# Revit family: Lavabo için Geberit sifon, yatay çıkış_PRO_145876
name_source: partatom
category: Pipe Fittings
revit_build: Autodesk Revit 2018 (Build: 20190510_1515(x64)
units: mm (PartAtom-declared; Revit-internal decimal feet)

## family parameters
Always vertical = Yes
Cut with Voids When Loaded = No
OmniClass Number = 23.60.30.11.14
OmniClass Title = Pipework Fittings
Part Type = Multi Port
Round Connector Dimension = Use Diameter
Shared = No
Work Plane-Based = No

## types (2) — shared parameters
Application purposes = Lavabolar için
Application range = Waste fittings
BIM Content Version = GEB MG 1.2
BIM Content revision date = 2020.04.28
Brand = Geberit
CW Connection = No
Characteristics = EN 274-3 uyarınca kalite kontrollü
Korozyona dayanıklı
Yatay çıkış
Connection diameter 1 = 30 mm  [stored 0.0984252 ft]
Description = Lavabo için Geberit sifon, yatay çıkış
GEB_culture = tr-TR
GEB_generic_description = washbasin trap
GEB_generic_manufacturer = generic
GEB_generic_model = washbasin trap
GEB_imperial_engineering = No
GEB_key_rules = 1000 [Articles.ArticlesList.Key] 
2000 [Name], d[ATT_10935]mm/G[ATT_10948]"
3000 [ATT_10673]
GEB_metric_engineering = Yes
GEB_pimversion = 22.02.12
GEB_processing_type = T
GEB_reference = PRO_145876
GEB_translations = {"applicationPurposes":"Application purposes","application_range":"Application range","brandName":"Brand","characteristics":"Characteristics","content_creator":"BIM Content creator","content_date_changed":"BIM Content revision date","content_version":"BIM Content Version","key 1000":"Article number key","ATT_10673":"EAN code basic data","name":"Name","productBrand":"Product brand","type":"Type","GEB_connection_diameter1":"Connection diameter 1","GEB_connection_diameter2":"Connection diameter 2","fixed_material":"Main material","ATT_10935":"d, ø","GEB_accessories":"Accessories"}
GEB_use_DN = Yes
HW Connection = No
IfcDescription = Lavabo için Geberit sifon, yatay çıkış
IfcExportAs = IfcPipeFitting
IfcExportType = ENTRY
LOD300 = No
LOD400 = Yes
Main material = Geberit_Plastic, White
Manufacturer = Geberit
Model = d40-G1 1/4''
Name = Lavabo için Geberit sifon, yatay çıkış
Type = d40-G1 1/4''
Vent Connection = No
Waste Connection = Yes
size_table = waste_ODDN_sizes
type_index = 1
zero-valued in all types: WFU

## per-type parameters (varying)
| type | Article number key | Connection diameter 2 | EAN code basic data | d, ø |
| 151.034.21.1 Lavabo için Geberit sifon, yatay çıkış | 151.034.21.1 | 32 mm  [stored 0.104987 ft] | 4025416706328 | 32 mm  [stored 0.104987 ft] |
| 151.035.21.1 Lavabo için Geberit sifon, yatay çıkış | 151.035.21.1 | 40 mm  [stored 0.131234 ft] | 4025416706342 | 40 mm  [stored 0.131234 ft] |

note: [stored X ft] marks values corroborated as IEEE doubles in the binary element streams (Revit-internal decimal feet)

## geometry (parser evidence)
native form markers: Blend x2, Sweep x1
no freeform markers — native parametric forms only
